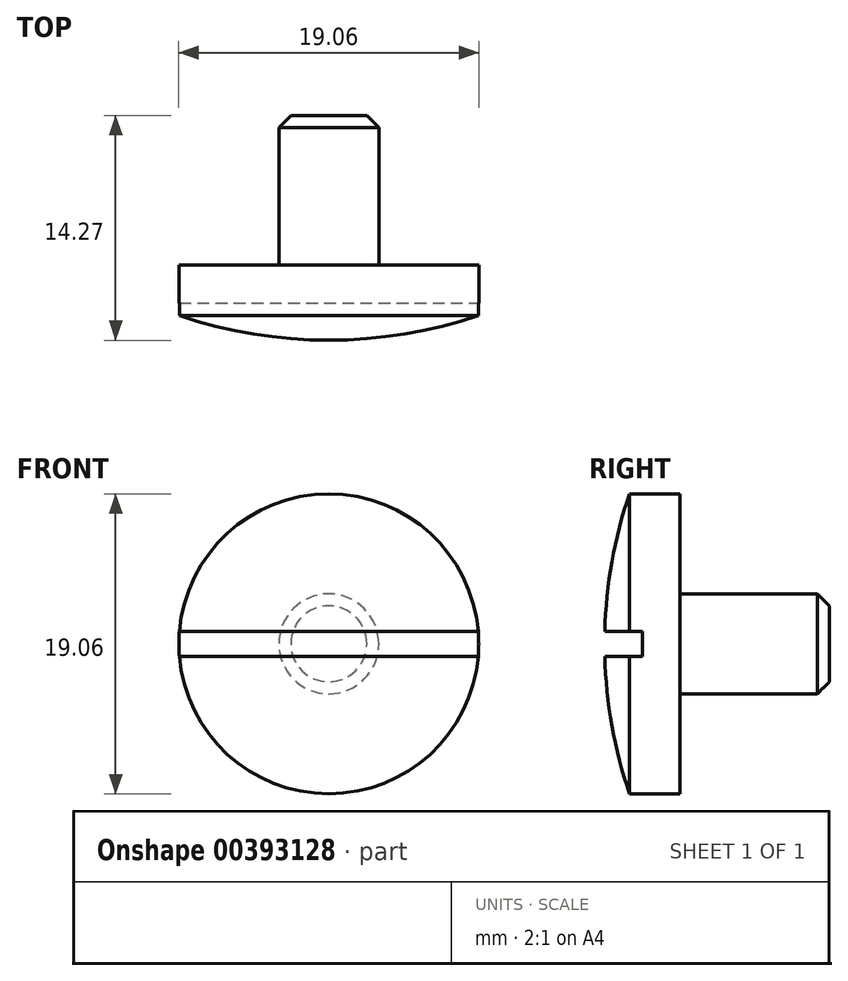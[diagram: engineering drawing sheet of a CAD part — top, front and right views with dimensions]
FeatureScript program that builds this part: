
annotation { "Feature Type Name" : "Feature", "Feature Type Description" : "" }
export const myFeature = defineFeature(function(context is Context, id is Id, definition is map)
    precondition{}
    {
        {
            var Q0;
            Q0=qCreatedBy(makeId("Right.planeOp"),FACE);
            var sketch = newSketch(context, id + "F0", { "sketchPlane" : qUnion([Q0])});
            skLineSegment(sketch, "E0", {"start": v(-7.14, 0) * mm, "end": v(7.14, 0) * mm});
            skLineSegment(sketch, "E1", {"start": v(7.14, 0) * mm, "end": v(7.14, 3.18) * mm});
            skLineSegment(sketch, "E2", {"start": v(7.14, 3.18) * mm, "end": v(-2.36, 3.18) * mm});
            skLineSegment(sketch, "E3", {"start": v(-2.36, 3.18) * mm, "end": v(-2.36, 9.53) * mm});
            skLineSegment(sketch, "E4", {"start": v(-2.36, 9.53) * mm, "end": v(-5.56, 9.53) * mm});
            skLineSegment(sketch, "E5", {"start": v(-7.14, 0) * mm, "end": v(-7.14, 9.53) * mm, "construction": true});
            skLineSegment(sketch, "E6", {"start": v(-5.56, 9.53) * mm, "end": v(-7.14, 9.53) * mm, "construction": true});
            skArc(sketch, "E7", {"start": v(-5.56, 9.52) * mm, "mid": v(-6.74, 4.83) * mm, "end": v(-7.14, 0) * mm});
            skSolve(sketch);
        }
        {
            var Q0;
            Q0=makeQuery(id+"F0.imprint","IMPRINT",FACE,{"disambiguationData":[TD([[makeQuery(id+"F0.imprint","IMPRINT",EDGE,{"derivedFrom":sQuery(id+"F0.wireOp",EDGE,"E0")}),1.0]])]});
            var Q1;
            Q1=sQuery(id+"F0.wireOp",EDGE,"E0");
            revolve(context, id + "F1", {"entities" : qUnion([Q0]), "axis" : qUnion([Q1]), "revolveType" : RevolveType.FULL});
        }
        {
            var Q0;
            Q0=qCreatedBy(makeId("Front.planeOp"),FACE);
            cPlane(context, id + "F2", {"entities" : qUnion([Q0]), "cplaneType" : CPlaneType.OFFSET, "offset" : 7.14 * mm, "width" : 152.4 * mm, "height" : 152.4 * mm});
        }
        {
            var Q0;
            Q0=qCreatedBy(id+"F2.planeOp",FACE);
            var sketch = newSketch(context, id + "F3", { "sketchPlane" : qUnion([Q0])});
            skArc(sketch, "E8", {"start": v(-9.5, 0.79) * mm, "mid": v(-9.53, 0) * mm, "end": v(-9.5, -0.79) * mm});
            skLineSegment(sketch, "E9", {"start": v(-9.5, 0.79) * mm, "end": v(9.5, 0.79) * mm});
            skLineSegment(sketch, "E10", {"start": v(-9.5, -0.79) * mm, "end": v(9.5, -0.79) * mm});
            skArc(sketch, "E11.trimOffspring", {"start": v(9.5, -0.79) * mm, "mid": v(9.53, 0) * mm, "end": v(9.5, 0.79) * mm});
            skSolve(sketch);
        }
        {
            var Q0;
            Q0 = qSketchRegion(id + "F3", true);
            extrude(context, id + "F4", {"entities" : qUnion([Q0]), "operationType" : NewBodyOperationType.REMOVE, "oppositeDirection" : true, "depth" : 2.4 * mm});
        }
        {
            var Q0;
            Q0=makeQuery(id+"F1.opRevolve","SWEPT_EDGE",EDGE,{"disambiguationData":[OSD([sQuery(id+"F0.wireOp",EDGE,"E1"),sQuery(id+"F0.wireOp",EDGE,"E2")])]});
            chamfer(context, id + "F5", {"entities" : qUnion([Q0]), "chamferType" : ChamferType.OFFSET_ANGLE, "width" : 0.76 * mm, "oppositeDirection" : false, "angle" : 45 * degree, "tangentPropagation" : true});
        }
    });
